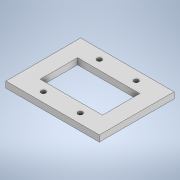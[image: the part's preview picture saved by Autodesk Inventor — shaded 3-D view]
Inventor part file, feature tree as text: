
AUTODESK INVENTOR PART (.ipt)
format: ipt  version: 2022 (Build 260153000, 153)  size: 115,200 bytes
history: native  units: mm
features: extrude x1, sketch x1
ambient origin geometry x8: Origin, YZ Plane, XZ Plane, XY Plane, X Axis, Y Axis, Z Axis, Center Point
bodies: Solid1 (feature_tree)
feature tree (2):
  extrude  "Extrusion1"  Depth=12.0mm
  sketch  "Sketch1"  dims[d0=15.0mm d1=12.0mm d2=10.0mm d3=6.0mm d4=2.5mm d5=3.0mm d6=0.75mm d7=4.5125mm d8=1.5mm d9=20.0mm d11=5.925mm d12=20.0mm d14=8.985mm d17=1.0mm d18=0.0mm]
